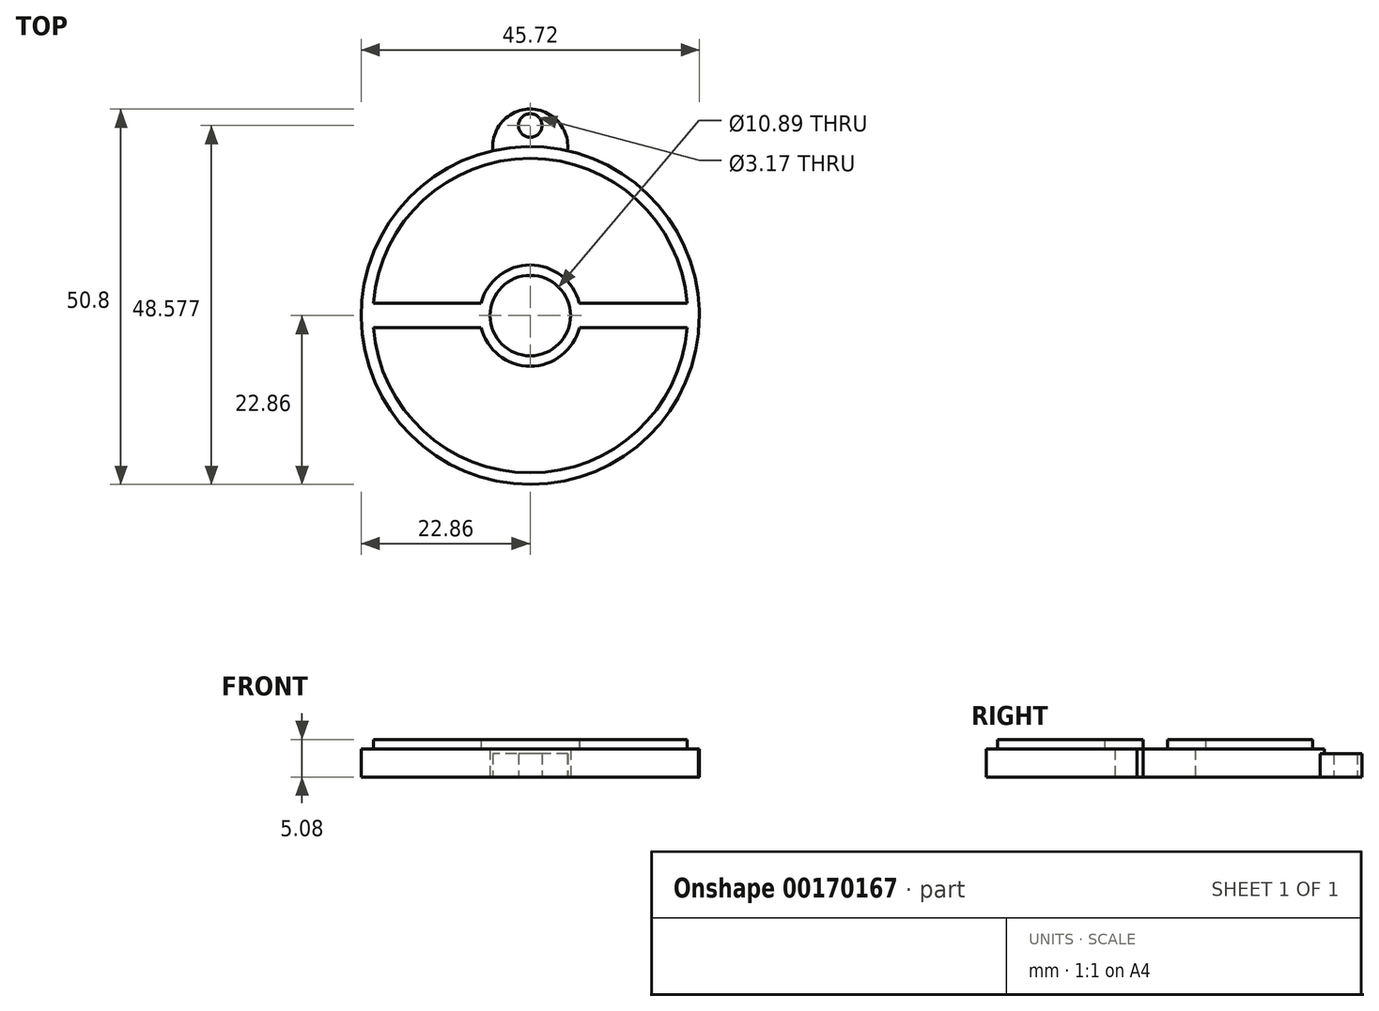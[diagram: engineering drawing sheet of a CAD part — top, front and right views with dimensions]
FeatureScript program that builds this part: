
annotation { "Feature Type Name" : "Feature", "Feature Type Description" : "" }
export const myFeature = defineFeature(function(context is Context, id is Id, definition is map)
    precondition{}
    {
        {
            var Q0;
            Q0=qCreatedBy(makeId("Top.planeOp"),FACE);
            var sketch = newSketch(context, id + "F0", { "sketchPlane" : qUnion([Q0])});
            skCircle(sketch, "E0", {"center": v(0, 0) * mm, "radius": 22.86 * mm});
            skLineSegment(sketch, "E1", {"start": v(-22.86, 0) * mm, "end": v(-22.71, 0) * mm});
            skLineSegment(sketch, "E2.bottom", {"start": v(-21.17, -1.63) * mm, "end": v(-6.65, -1.63) * mm});
            skLineSegment(sketch, "E2.top", {"start": v(-21.17, 1.7) * mm, "end": v(-6.63, 1.7) * mm});
            skLineSegment(sketch, "E2.right", {"start": v(22.73, -2.48) * mm, "end": v(22.73, -1.63) * mm});
            skCircle(sketch, "E3", {"center": v(0, 0) * mm, "radius": 5.44 * mm});
            skArc(sketch, "E4", {"start": v(-6.65, -1.63) * mm, "mid": v(0, -6.85) * mm, "end": v(6.65, -1.63) * mm});
            skLineSegment(sketch, "E5.trimOffspring", {"start": v(6.63, 1.7) * mm, "end": v(21.17, 1.7) * mm});
            skLineSegment(sketch, "E6.trimOffspring", {"start": v(22.73, 0) * mm, "end": v(22.86, 0) * mm});
            skLineSegment(sketch, "E7.trimOffspring", {"start": v(6.65, -1.63) * mm, "end": v(21.17, -1.63) * mm});
            skArc(sketch, "E8.trimOffspring", {"start": v(6.63, 1.7) * mm, "mid": v(0, 6.85) * mm, "end": v(-6.63, 1.7) * mm});
            skLineSegment(sketch, "E9.trimOffspring", {"start": v(22.73, -1.63) * mm, "end": v(22.8, -1.63) * mm});
            skCircle(sketch, "E10", {"center": v(0, 0) * mm, "radius": 4.54 * mm});
            skLineSegment(sketch, "E11", {"start": v(-21.17, 1.7) * mm, "end": v(-21.22, 1.7) * mm});
            skLineSegment(sketch, "E12", {"start": v(-21.17, -1.63) * mm, "end": v(-21.22, -1.63) * mm});
            skLineSegment(sketch, "E13", {"start": v(21.17, -1.63) * mm, "end": v(21.22, -1.63) * mm});
            skLineSegment(sketch, "E14", {"start": v(21.17, 1.7) * mm, "end": v(21.22, 1.7) * mm});
            skArc(sketch, "E15", {"start": v(-21.22, -1.63) * mm, "mid": v(0, -21.29) * mm, "end": v(21.22, -1.63) * mm});
            skArc(sketch, "E16.trimOffspring", {"start": v(21.22, 1.7) * mm, "mid": v(0, 21.29) * mm, "end": v(-21.22, 1.7) * mm});
            skLineSegment(sketch, "E17.trimOffspring", {"start": v(22.8, 1.7) * mm, "end": v(22.8, 1.7) * mm});
            skArc(sketch, "E18", {"start": v(5.05, 22.3) * mm, "mid": v(0, 27.94) * mm, "end": v(-5.05, 22.3) * mm});
            skPoint(sketch, "E18.centerSnap0", {"position": v(0, 21.29) * mm});
            skCircle(sketch, "E19", {"center": v(0, 25.72) * mm, "radius": 1.59 * mm});
            skSolve(sketch);
        }
        {
            var Q0;
            Q0=makeQuery(id+"F0.imprint","IMPRINT",FACE,{"disambiguationData":[TD([[makeQuery(id+"F0.imprint","IMPRINT",EDGE,{"derivedFrom":sQuery(id+"F0.wireOp",EDGE,"E2.top")}),1.0]])]});
            var Q1;
            Q1=makeQuery(id+"F0.imprint","IMPRINT",FACE,{"disambiguationData":[TD([[makeQuery(id+"F0.imprint","IMPRINT",EDGE,{"derivedFrom":sQuery(id+"F0.wireOp",EDGE,"E2.bottom")}),-1.0]])]});
            extrude(context, id + "F1", {"entities" : qUnion([Q0, Q1]), "depth" : 5.08 * mm});
        }
        {
            var Q0;
            Q0=makeQuery(id+"F0.imprint","IMPRINT",FACE,{"disambiguationData":[TD([[makeQuery(id+"F0.imprint","IMPRINT",EDGE,{"derivedFrom":sQuery(id+"F0.wireOp",EDGE,"E2.bottom")}),1.0]])]});
            extrude(context, id + "F2", {"entities" : qUnion([Q0]), "operationType" : NewBodyOperationType.ADD, "depth" : 3.8 * mm});
        }
        {
            var Q0;
            {var subQ0=sQuery(id+"F0.wireOp",EDGE,"E18");Q0=makeQuery(id+"F0.imprint","IMPRINT",FACE,{"disambiguationData":[TD([[makeQuery(id+"F0.imprint","IMPRINT",EDGE,{"derivedFrom":subQ0}),1.0]])]});}
            extrude(context, id + "F3", {"entities" : qUnion([Q0]), "operationType" : NewBodyOperationType.ADD, "depth" : 3.17 * mm});
        }
    });
